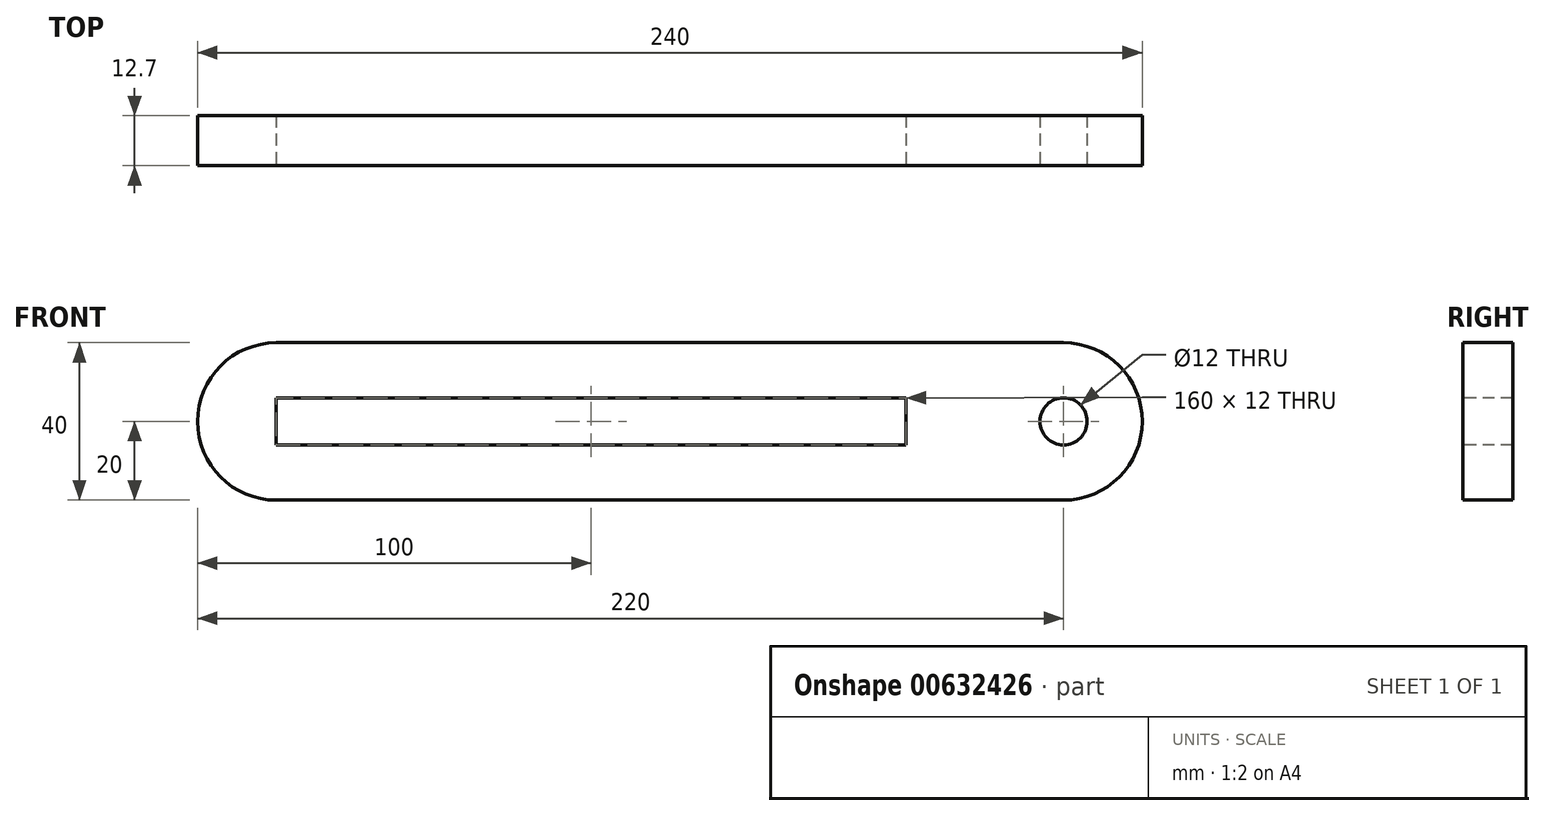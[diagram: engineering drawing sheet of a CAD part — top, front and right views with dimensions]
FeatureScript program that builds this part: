
annotation { "Feature Type Name" : "Feature", "Feature Type Description" : "" }
export const myFeature = defineFeature(function(context is Context, id is Id, definition is map)
    precondition{}
    {
        {
            var Q0;
            Q0=qCreatedBy(makeId("Front.planeOp"),FACE);
            var sketch = newSketch(context, id + "F0", { "sketchPlane" : qUnion([Q0])});
            skLineSegment(sketch, "E0", {"start": v(0, 20) * mm, "end": v(200, 20) * mm});
            skLineSegment(sketch, "E1", {"start": v(0, -20) * mm, "end": v(200, -20) * mm});
            skArc(sketch, "E2", {"start": v(200, -20) * mm, "mid": v(220, 0) * mm, "end": v(200, 20) * mm});
            skArc(sketch, "E3", {"start": v(0, 20) * mm, "mid": v(-20, 0) * mm, "end": v(0, -20) * mm});
            skCircle(sketch, "E4", {"center": v(200, 0) * mm, "radius": 6 * mm});
            skLineSegment(sketch, "E5.bottom", {"start": v(0, 6) * mm, "end": v(160, 6) * mm});
            skLineSegment(sketch, "E5.top", {"start": v(0, -6) * mm, "end": v(160, -6) * mm});
            skLineSegment(sketch, "E5.left", {"start": v(0, 6) * mm, "end": v(0, -6) * mm});
            skLineSegment(sketch, "E5.right", {"start": v(160, 6) * mm, "end": v(160, -6) * mm});
            skLineSegment(sketch, "E6", {"start": v(0, 0) * mm, "end": v(200, 0) * mm, "construction": true});
            skSolve(sketch);
        }
        {
            var Q0;
            Q0=makeQuery(id+"F0.imprint","IMPRINT",FACE,{"disambiguationData":[TD([[makeQuery(id+"F0.imprint","IMPRINT",EDGE,{"derivedFrom":sQuery(id+"F0.wireOp",EDGE,"E0")}),-1.0]])]});
            extrude(context, id + "F1", {"entities" : qUnion([Q0]), "oppositeDirection" : true, "depth" : 12.7 * mm, "offsetDistance" : 25 * mm});
        }
    });
